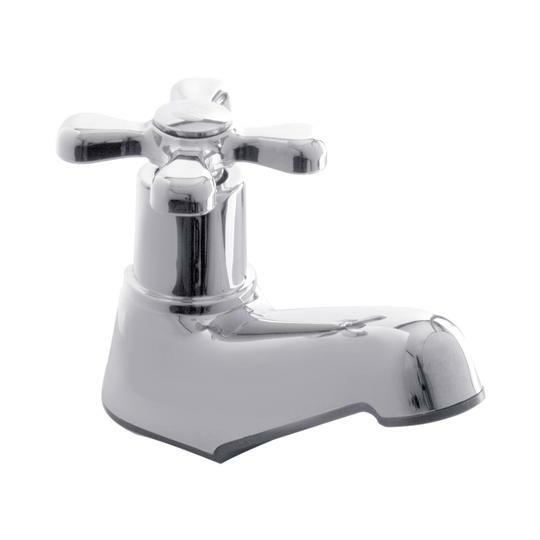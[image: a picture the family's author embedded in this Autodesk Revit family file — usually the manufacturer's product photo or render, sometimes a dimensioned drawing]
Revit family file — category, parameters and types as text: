
# Revit family: 01-1300-11 LLAVE INDIVIDUAL LAVAMANOS ATLANTICO
name_source: partatom
category: Plumbing Fixtures
revit_build: Autodesk Revit 2018 (Build: 20170223_1515(x64)
units: mm (PartAtom-declared; Revit-internal decimal feet)

## family parameters
Cut with Voids When Loaded = No
Host = Face
OmniClass Number = 23.31.11.00
Part Type = Normal
Room Calculation Point = No
Round Connector Dimension = Use Diameter
Shared = No

## types (1)
- 01-1300-11
    Alto = 80 mm  [stored 0.262467 ft]
    CW Connection = Yes
    Default Elevation = 0 mm  [stored 0 ft]
    Description = Llave individual
    Eje - Aireador = 81 mm
    HW Connection = Yes
    Link Ficha Tecnica = http://infotecnica.gricol.com
    Manija = 66 mm  [stored 0.216535 ft]
    Manufacturer = Gricol
    Model = 01-1300-11
    Plastico - ABS Cromado = Plastico - ABS Cromado
    Product Name = LLAVE INDIVIDUAL LAVAMANOS ATLANTICO
    Type Image = LLAVE INDIVIDUAL LAVAMANOS ATLANTICO.jpg
    URL = https://www.gricol.com
    Vent Connection = No
    Waste Connection = No

note: [stored X ft] marks values corroborated as IEEE doubles in the binary element streams (Revit-internal decimal feet)

## geometry (parser evidence)
native form markers: Blend x2, Sweep x4
no freeform markers — native parametric forms only
